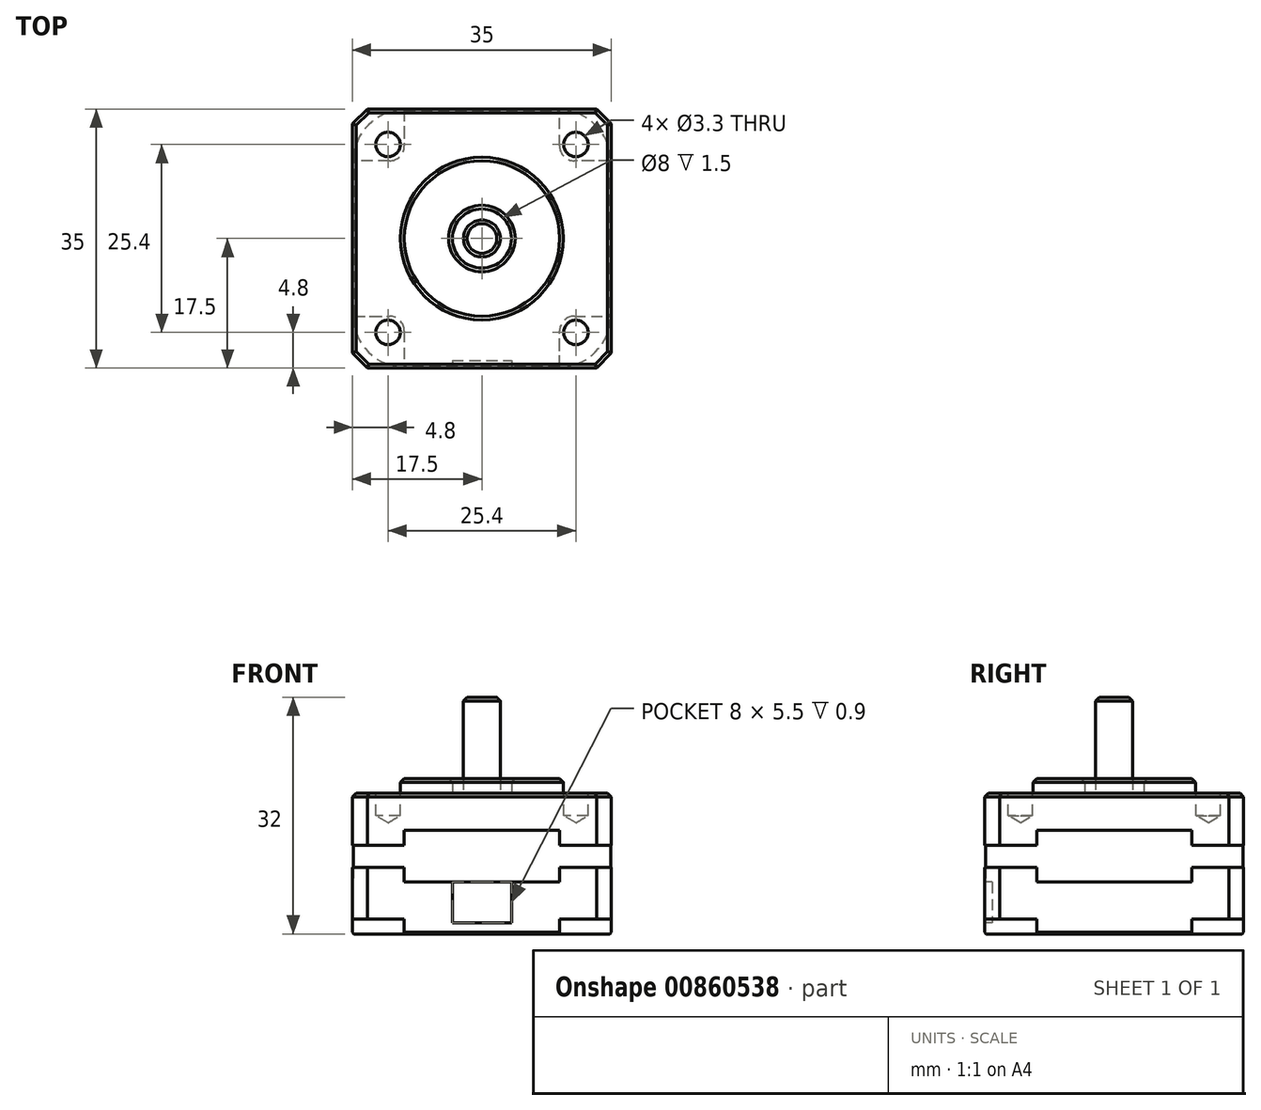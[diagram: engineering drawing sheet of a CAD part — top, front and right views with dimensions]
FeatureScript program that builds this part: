
annotation { "Feature Type Name" : "Feature", "Feature Type Description" : "" }
export const myFeature = defineFeature(function(context is Context, id is Id, definition is map)
    precondition{}
    {
        {
            var Q0;
            Q0=qCreatedBy(makeId("Top.planeOp"),FACE);
            var sketch = newSketch(context, id + "F0", { "sketchPlane" : qUnion([Q0])});
            skLineSegment(sketch, "E0.bottom", {"start": v(-17.5, 17.5) * mm, "end": v(17.5, 17.5) * mm});
            skLineSegment(sketch, "E0.top", {"start": v(-17.5, -17.5) * mm, "end": v(17.5, -17.5) * mm});
            skLineSegment(sketch, "E0.left", {"start": v(-17.5, 17.5) * mm, "end": v(-17.5, -17.5) * mm});
            skLineSegment(sketch, "E0.right", {"start": v(17.5, 17.5) * mm, "end": v(17.5, -17.5) * mm});
            skSolve(sketch);
        }
        {
            var Q0;
            Q0=makeQuery(id+"F0.imprint","IMPRINT",FACE,{"disambiguationData":[TD([[makeQuery(id+"F0.imprint","IMPRINT",EDGE,{"derivedFrom":sQuery(id+"F0.wireOp",EDGE,"E0.bottom")}),-1.0]])]});
            extrude(context, id + "F1", {"entities" : qUnion([Q0]), "depth" : 5 * mm, "offsetDistance" : 25 * mm});
        }
        {
            var Q0;
            Q0=makeQuery(id+"F1.opExtrude","CAP_FACE",FACE,{"disambiguationData":[OSD([sQuery(id+"F0.wireOp",EDGE,"E0.bottom"),sQuery(id+"F0.wireOp",EDGE,"E0.top"),sQuery(id+"F0.wireOp",EDGE,"E0.left"),sQuery(id+"F0.wireOp",EDGE,"E0.right")])],"isStart":false});
            var sketch = newSketch(context, id + "F2", { "sketchPlane" : qUnion([Q0])});
            skCircle(sketch, "E1", {"center": v(0, 0) * mm, "radius": 11 * mm});
            skCircle(sketch, "E2", {"center": v(0, 0) * mm, "radius": 4 * mm});
            skSolve(sketch);
        }
        {
            var Q0;
            Q0=makeQuery(id+"F2.imprint","IMPRINT",FACE,{"disambiguationData":[TD([[makeQuery(id+"F2.imprint","IMPRINT",EDGE,{"derivedFrom":sQuery(id+"F2.wireOp",EDGE,"E1")}),1.0]])]});
            extrude(context, id + "F3", {"entities" : qUnion([Q0]), "operationType" : NewBodyOperationType.ADD, "depth" : 2 * mm, "offsetDistance" : 25 * mm});
        }
        {
            var Q0;
            Q0=makeQuery(id+"F1.opExtrude","SWEPT_EDGE",EDGE,{"disambiguationData":[OSD([sQuery(id+"F0.wireOp",EDGE,"E0.bottom"),sQuery(id+"F0.wireOp",EDGE,"E0.left")])]});
            var Q1;
            Q1=makeQuery(id+"F1.opExtrude","SWEPT_EDGE",EDGE,{"disambiguationData":[OSD([sQuery(id+"F0.wireOp",EDGE,"E0.top"),sQuery(id+"F0.wireOp",EDGE,"E0.left")])]});
            var Q2;
            Q2=makeQuery(id+"F1.opExtrude","SWEPT_EDGE",EDGE,{"disambiguationData":[OSD([sQuery(id+"F0.wireOp",EDGE,"E0.top"),sQuery(id+"F0.wireOp",EDGE,"E0.right")])]});
            var Q3;
            Q3=makeQuery(id+"F1.opExtrude","SWEPT_EDGE",EDGE,{"disambiguationData":[OSD([sQuery(id+"F0.wireOp",EDGE,"E0.bottom"),sQuery(id+"F0.wireOp",EDGE,"E0.right")])]});
            chamfer(context, id + "F4", {"entities" : qUnion([Q0, Q1, Q2, Q3]), "width" : 2 * mm, "tangentPropagation" : true});
        }
        {
            var Q0;
            Q0=makeQuery(id+"F3.boolean.opBoolean","SPLIT",FACE,{"disambiguationData":[TD([makeQuery(id+"F3.opExtrude","SWEPT_FACE",FACE,{"disambiguationData":[OSD([sQuery(id+"F2.wireOp",EDGE,"E2")])]})])],"derivedFrom":makeQuery(id+"F1.opExtrude","CAP_FACE",FACE,{"disambiguationData":[OSD([sQuery(id+"F0.wireOp",EDGE,"E0.bottom"),sQuery(id+"F0.wireOp",EDGE,"E0.top"),sQuery(id+"F0.wireOp",EDGE,"E0.left"),sQuery(id+"F0.wireOp",EDGE,"E0.right")])],"isStart":false})});
            var sketch = newSketch(context, id + "F5", { "sketchPlane" : qUnion([Q0])});
            skCircle(sketch, "E3", {"center": v(0, 0) * mm, "radius": 2.5 * mm});
            skSolve(sketch);
        }
        {
            var Q0;
            Q0=makeQuery(id+"F5.imprint","IMPRINT",FACE,{"disambiguationData":[TD([[makeQuery(id+"F5.imprint","IMPRINT",EDGE,{"derivedFrom":sQuery(id+"F5.wireOp",EDGE,"E3")}),1.0]])]});
            extrude(context, id + "F6", {"entities" : qUnion([Q0]), "operationType" : NewBodyOperationType.ADD, "depth" : 13 * mm, "offsetDistance" : 25 * mm});
        }
        {
            var Q0;
            {var subQ0=sQuery(id+"F0.wireOp",EDGE,"E0.left");var subQ1=sQuery(id+"F0.wireOp",EDGE,"E0.top");var subQ2=sQuery(id+"F0.wireOp",EDGE,"E0.right");var subQ3=sQuery(id+"F0.wireOp",EDGE,"E0.bottom");Q0=makeQuery(id+"F3.boolean.opBoolean","SPLIT",FACE,{"disambiguationData":[TD([makeQuery(id+"F1.opExtrude","SWEPT_FACE",FACE,{"disambiguationData":[OSD([subQ3])]})])],"derivedFrom":makeQuery(id+"F1.opExtrude","CAP_FACE",FACE,{"disambiguationData":[OSD([subQ3,subQ1,subQ0,subQ2])],"isStart":false})});}
            var sketch = newSketch(context, id + "F7", { "sketchPlane" : qUnion([Q0])});
            skPoint(sketch, "E4", {"position": v(-12.7, -12.7) * mm});
            skPoint(sketch, "E5", {"position": v(-12.7, 12.7) * mm});
            skPoint(sketch, "E6", {"position": v(12.7, 12.7) * mm});
            skPoint(sketch, "E7", {"position": v(12.7, -12.7) * mm});
            skSolve(sketch);
        }
        {
            var Q0;
            Q0=sQuery(id+"F7.wireOp",VERTEX,"E4");
            var Q1;
            Q1=sQuery(id+"F7.wireOp",VERTEX,"E5");
            var Q2;
            Q2=sQuery(id+"F7.wireOp",VERTEX,"E6");
            var Q3;
            Q3=sQuery(id+"F7.wireOp",VERTEX,"E7");
            var Q4;
            Q4=makeQuery(id+"F1.opExtrude","SWEPT_BODY",BODY,{"disambiguationData":[OSD([sQuery(id+"F0.wireOp",EDGE,"E0.bottom"),sQuery(id+"F0.wireOp",EDGE,"E0.top"),sQuery(id+"F0.wireOp",EDGE,"E0.left"),sQuery(id+"F0.wireOp",EDGE,"E0.right")])]});
            hole(context, id + "F8", {"style" : HoleStyle.SIMPLE, "endStyle" : HoleEndStyle.BLIND, "standardTappedOrClearance" : lookupTablePath({ "standard" : "ISO", "engagement" : "75%", "pitch" : "0.7 mm", "size" : "M4", "type" : "Tapped" }), "standardBlindInLast" : lookupTablePath({ "standard" : "ISO", "engagement" : "75%", "pitch" : "0.7 mm", "size" : "M4", "type" : "Tapped" }), "holeDiameter" : 3.3 * mm, "majorDiameter" : 4 * mm, "showTappedDepth" : true, "holeDepth" : 3 * mm, "isTappedThrough" : true, "tappedDepth" : 0.9 * mm, "tapClearance" : 3, "locations" : qUnion([Q0, Q1, Q2, Q3]), "scope" : qUnion([Q4])});
        }
        {
            var Q0;
            Q0=makeQuery(id+"F1.opExtrude","CAP_EDGE",EDGE,{"disambiguationData":[OSD([sQuery(id+"F0.wireOp",EDGE,"E0.top")])],"isStart":false});
            var Q1;
            Q1=makeQuery(id+"F1.opExtrude","CAP_EDGE",EDGE,{"disambiguationData":[OSD([sQuery(id+"F0.wireOp",EDGE,"E0.left")])],"isStart":false});
            var Q2;
            Q2=makeQuery(id+"F1.opExtrude","CAP_EDGE",EDGE,{"disambiguationData":[OSD([sQuery(id+"F0.wireOp",EDGE,"E0.bottom")])],"isStart":false});
            var Q3;
            Q3=makeQuery(id+"F1.opExtrude","CAP_EDGE",EDGE,{"disambiguationData":[OSD([sQuery(id+"F0.wireOp",EDGE,"E0.right")])],"isStart":false});
            var Q4;
            {var subQ0=sQuery(id+"F0.wireOp",EDGE,"E0.left");var subQ1=sQuery(id+"F0.wireOp",EDGE,"E0.top");var subQ2=sQuery(id+"F0.wireOp",EDGE,"E0.right");var subQ3=sQuery(id+"F0.wireOp",EDGE,"E0.bottom");Q4=makeQuery(id+"F4.opChamfer","BLEND_EDGE",EDGE,{"blendedFrom":[makeQuery(id+"F1.opExtrude","SWEPT_EDGE",EDGE,{"disambiguationData":[OSD([subQ1,subQ2])]}),makeQuery(id+"F3.boolean.opBoolean","SPLIT",FACE,{"disambiguationData":[TD([makeQuery(id+"F1.opExtrude","SWEPT_FACE",FACE,{"disambiguationData":[OSD([subQ3])]})])],"derivedFrom":makeQuery(id+"F1.opExtrude","CAP_FACE",FACE,{"disambiguationData":[OSD([subQ3,subQ1,subQ0,subQ2])],"isStart":false})})],"blendedInto":[makeQuery(id+"F3.boolean.opBoolean","SPLIT",FACE,{"disambiguationData":[TD([makeQuery(id+"F1.opExtrude","SWEPT_FACE",FACE,{"disambiguationData":[OSD([subQ3])]})])],"derivedFrom":makeQuery(id+"F1.opExtrude","CAP_FACE",FACE,{"disambiguationData":[OSD([subQ3,subQ1,subQ0,subQ2])],"isStart":false})})]});}
            var Q5;
            {var subQ0=sQuery(id+"F0.wireOp",EDGE,"E0.left");var subQ1=sQuery(id+"F0.wireOp",EDGE,"E0.top");var subQ2=sQuery(id+"F0.wireOp",EDGE,"E0.right");var subQ3=sQuery(id+"F0.wireOp",EDGE,"E0.bottom");Q5=makeQuery(id+"F4.opChamfer","BLEND_EDGE",EDGE,{"blendedFrom":[makeQuery(id+"F1.opExtrude","SWEPT_EDGE",EDGE,{"disambiguationData":[OSD([subQ3,subQ2])]}),makeQuery(id+"F3.boolean.opBoolean","SPLIT",FACE,{"disambiguationData":[TD([makeQuery(id+"F1.opExtrude","SWEPT_FACE",FACE,{"disambiguationData":[OSD([subQ3])]})])],"derivedFrom":makeQuery(id+"F1.opExtrude","CAP_FACE",FACE,{"disambiguationData":[OSD([subQ3,subQ1,subQ0,subQ2])],"isStart":false})})],"blendedInto":[makeQuery(id+"F3.boolean.opBoolean","SPLIT",FACE,{"disambiguationData":[TD([makeQuery(id+"F1.opExtrude","SWEPT_FACE",FACE,{"disambiguationData":[OSD([subQ3])]})])],"derivedFrom":makeQuery(id+"F1.opExtrude","CAP_FACE",FACE,{"disambiguationData":[OSD([subQ3,subQ1,subQ0,subQ2])],"isStart":false})})]});}
            var Q6;
            {var subQ0=sQuery(id+"F0.wireOp",EDGE,"E0.left");var subQ1=sQuery(id+"F0.wireOp",EDGE,"E0.top");var subQ2=sQuery(id+"F0.wireOp",EDGE,"E0.right");var subQ3=sQuery(id+"F0.wireOp",EDGE,"E0.bottom");Q6=makeQuery(id+"F4.opChamfer","BLEND_EDGE",EDGE,{"blendedFrom":[makeQuery(id+"F1.opExtrude","SWEPT_EDGE",EDGE,{"disambiguationData":[OSD([subQ3,subQ0])]}),makeQuery(id+"F3.boolean.opBoolean","SPLIT",FACE,{"disambiguationData":[TD([makeQuery(id+"F1.opExtrude","SWEPT_FACE",FACE,{"disambiguationData":[OSD([subQ3])]})])],"derivedFrom":makeQuery(id+"F1.opExtrude","CAP_FACE",FACE,{"disambiguationData":[OSD([subQ3,subQ1,subQ0,subQ2])],"isStart":false})})],"blendedInto":[makeQuery(id+"F3.boolean.opBoolean","SPLIT",FACE,{"disambiguationData":[TD([makeQuery(id+"F1.opExtrude","SWEPT_FACE",FACE,{"disambiguationData":[OSD([subQ3])]})])],"derivedFrom":makeQuery(id+"F1.opExtrude","CAP_FACE",FACE,{"disambiguationData":[OSD([subQ3,subQ1,subQ0,subQ2])],"isStart":false})})]});}
            var Q7;
            {var subQ0=sQuery(id+"F0.wireOp",EDGE,"E0.left");var subQ1=sQuery(id+"F0.wireOp",EDGE,"E0.top");var subQ2=sQuery(id+"F0.wireOp",EDGE,"E0.right");var subQ3=sQuery(id+"F0.wireOp",EDGE,"E0.bottom");Q7=makeQuery(id+"F4.opChamfer","BLEND_EDGE",EDGE,{"blendedFrom":[makeQuery(id+"F1.opExtrude","SWEPT_EDGE",EDGE,{"disambiguationData":[OSD([subQ1,subQ0])]}),makeQuery(id+"F3.boolean.opBoolean","SPLIT",FACE,{"disambiguationData":[TD([makeQuery(id+"F1.opExtrude","SWEPT_FACE",FACE,{"disambiguationData":[OSD([subQ3])]})])],"derivedFrom":makeQuery(id+"F1.opExtrude","CAP_FACE",FACE,{"disambiguationData":[OSD([subQ3,subQ1,subQ0,subQ2])],"isStart":false})})],"blendedInto":[makeQuery(id+"F3.boolean.opBoolean","SPLIT",FACE,{"disambiguationData":[TD([makeQuery(id+"F1.opExtrude","SWEPT_FACE",FACE,{"disambiguationData":[OSD([subQ3])]})])],"derivedFrom":makeQuery(id+"F1.opExtrude","CAP_FACE",FACE,{"disambiguationData":[OSD([subQ3,subQ1,subQ0,subQ2])],"isStart":false})})]});}
            var Q8;
            Q8=makeQuery(id+"F3.opExtrude","CAP_EDGE",EDGE,{"disambiguationData":[OSD([sQuery(id+"F2.wireOp",EDGE,"E1")])],"isStart":false});
            var Q9;
            Q9=makeQuery(id+"F3.opExtrude","CAP_EDGE",EDGE,{"disambiguationData":[OSD([sQuery(id+"F2.wireOp",EDGE,"E2")])],"isStart":false});
            var Q10;
            Q10=makeQuery(id+"F6.opExtrude","CAP_EDGE",EDGE,{"disambiguationData":[OSD([sQuery(id+"F5.wireOp",EDGE,"E3")])],"isStart":false});
            chamfer(context, id + "F9", {"entities" : qUnion([Q0, Q1, Q2, Q3, Q4, Q5, Q6, Q7, Q8, Q9, Q10]), "width" : 0.5 * mm, "tangentPropagation" : true});
        }
        {
            var Q0;
            Q0=makeQuery(id+"F1.opExtrude","CAP_FACE",FACE,{"disambiguationData":[OSD([sQuery(id+"F0.wireOp",EDGE,"E0.bottom"),sQuery(id+"F0.wireOp",EDGE,"E0.top"),sQuery(id+"F0.wireOp",EDGE,"E0.left"),sQuery(id+"F0.wireOp",EDGE,"E0.right")])],"isStart":true});
            var sketch = newSketch(context, id + "F10", { "sketchPlane" : qUnion([Q0])});
            skLineSegment(sketch, "E8.bottom", {"start": v(-10.4, 17.4) * mm, "end": v(10.4, 17.4) * mm});
            skLineSegment(sketch, "E8.top", {"start": v(-10.4, -17.4) * mm, "end": v(10.4, -17.4) * mm});
            skLineSegment(sketch, "E8.left", {"start": v(-17.4, 10.4) * mm, "end": v(-17.4, -10.4) * mm});
            skLineSegment(sketch, "E8.right", {"start": v(17.4, 10.4) * mm, "end": v(17.4, -10.4) * mm});
            skPoint(sketch, "E9.visualSharp", {"position": v(-17.4, 17.4) * mm});
            skArc(sketch, "E9.filletArc", {"start": v(-10.4, 17.4) * mm, "mid": v(-15.35, 15.35) * mm, "end": v(-17.4, 10.4) * mm});
            skPoint(sketch, "E10.visualSharp", {"position": v(17.4, 17.4) * mm});
            skArc(sketch, "E10.filletArc", {"start": v(17.4, 10.4) * mm, "mid": v(15.35, 15.35) * mm, "end": v(10.4, 17.4) * mm});
            skPoint(sketch, "E11.visualSharp", {"position": v(17.4, -17.4) * mm});
            skArc(sketch, "E11.filletArc", {"start": v(10.4, -17.4) * mm, "mid": v(15.35, -15.35) * mm, "end": v(17.4, -10.4) * mm});
            skPoint(sketch, "E12.visualSharp", {"position": v(-17.4, -17.4) * mm});
            skArc(sketch, "E12.filletArc", {"start": v(-17.4, -10.4) * mm, "mid": v(-15.35, -15.35) * mm, "end": v(-10.4, -17.4) * mm});
            skSolve(sketch);
        }
        {
            var Q0;
            Q0=makeQuery(id+"F10.imprint","IMPRINT",FACE,{"disambiguationData":[TD([[makeQuery(id+"F10.imprint","IMPRINT",EDGE,{"derivedFrom":sQuery(id+"F10.wireOp",EDGE,"E8.bottom")}),-1.0]])]});
            extrude(context, id + "F11", {"entities" : qUnion([Q0]), "operationType" : NewBodyOperationType.ADD, "depth" : 7 * mm, "offsetDistance" : 25 * mm});
        }
        {
            var Q0;
            Q0=makeQuery(id+"F1.opExtrude","CAP_FACE",FACE,{"disambiguationData":[OSD([sQuery(id+"F0.wireOp",EDGE,"E0.bottom"),sQuery(id+"F0.wireOp",EDGE,"E0.top"),sQuery(id+"F0.wireOp",EDGE,"E0.left"),sQuery(id+"F0.wireOp",EDGE,"E0.right")])],"isStart":true});
            var sketch = newSketch(context, id + "F12", { "sketchPlane" : qUnion([Q0])});
            skLineSegment(sketch, "E13.bottom", {"start": v(-17.5, 17.5) * mm, "end": v(-10.5, 17.5) * mm});
            skLineSegment(sketch, "E13.top", {"start": v(-17.5, 10.5) * mm, "end": v(-10.5, 10.5) * mm});
            skLineSegment(sketch, "E13.left", {"start": v(-17.5, 17.5) * mm, "end": v(-17.5, 10.5) * mm});
            skLineSegment(sketch, "E13.right", {"start": v(-10.5, 17.5) * mm, "end": v(-10.5, 10.5) * mm});
            skLineSegment(sketch, "E14", {"start": v(-17.5, 15.5) * mm, "end": v(-15.5, 17.5) * mm});
            skLineSegment(sketch, "E15.1.0", {"start": v(-15.5, -17.5) * mm, "end": v(-17.5, -15.5) * mm});
            skLineSegment(sketch, "E15.1.1", {"start": v(-17.5, -10.5) * mm, "end": v(-10.5, -10.5) * mm});
            skLineSegment(sketch, "E15.1.2", {"start": v(-17.5, -17.5) * mm, "end": v(-17.5, -10.5) * mm});
            skLineSegment(sketch, "E15.1.3", {"start": v(-17.5, -17.5) * mm, "end": v(-10.5, -17.5) * mm});
            skLineSegment(sketch, "E15.1.4", {"start": v(-10.5, -17.5) * mm, "end": v(-10.5, -10.5) * mm});
            skLineSegment(sketch, "E15.2.0", {"start": v(17.5, -15.5) * mm, "end": v(15.5, -17.5) * mm});
            skLineSegment(sketch, "E15.2.1", {"start": v(10.5, -17.5) * mm, "end": v(10.5, -10.5) * mm});
            skLineSegment(sketch, "E15.2.2", {"start": v(17.5, -17.5) * mm, "end": v(10.5, -17.5) * mm});
            skLineSegment(sketch, "E15.2.3", {"start": v(17.5, -17.5) * mm, "end": v(17.5, -10.5) * mm});
            skLineSegment(sketch, "E15.2.4", {"start": v(17.5, -10.5) * mm, "end": v(10.5, -10.5) * mm});
            skLineSegment(sketch, "E15.3.0", {"start": v(15.5, 17.5) * mm, "end": v(17.5, 15.5) * mm});
            skLineSegment(sketch, "E15.3.1", {"start": v(17.5, 10.5) * mm, "end": v(10.5, 10.5) * mm});
            skLineSegment(sketch, "E15.3.2", {"start": v(17.5, 17.5) * mm, "end": v(17.5, 10.5) * mm});
            skLineSegment(sketch, "E15.3.3", {"start": v(17.5, 17.5) * mm, "end": v(10.5, 17.5) * mm});
            skLineSegment(sketch, "E15.3.4", {"start": v(10.5, 17.5) * mm, "end": v(10.5, 10.5) * mm});
            skPoint(sketch, "E15.center", {"position": v(0, 0) * mm});
            skSolve(sketch);
        }
        {
            var Q0;
            {var subQ9=sQuery(id+"F12.wireOp",EDGE,"E14");Q0=makeQuery(id+"F12.imprint","IMPRINT",FACE,{"disambiguationData":[TD([[makeQuery(id+"F12.imprint","IMPRINT",EDGE,{"derivedFrom":subQ9}),1.0]])]});}
            var Q1;
            {var subQ1=sQuery(id+"F12.wireOp",EDGE,"E15.3.0");Q1=makeQuery(id+"F12.imprint","IMPRINT",FACE,{"disambiguationData":[TD([[makeQuery(id+"F12.imprint","IMPRINT",EDGE,{"derivedFrom":subQ1}),1.0]])]});}
            var Q2;
            {var subQ1=sQuery(id+"F12.wireOp",EDGE,"E15.2.0");Q2=makeQuery(id+"F12.imprint","IMPRINT",FACE,{"disambiguationData":[TD([[makeQuery(id+"F12.imprint","IMPRINT",EDGE,{"derivedFrom":subQ1}),1.0]])]});}
            var Q3;
            {var subQ1=sQuery(id+"F12.wireOp",EDGE,"E15.1.0");Q3=makeQuery(id+"F12.imprint","IMPRINT",FACE,{"disambiguationData":[TD([[makeQuery(id+"F12.imprint","IMPRINT",EDGE,{"derivedFrom":subQ1}),1.0]])]});}
            extrude(context, id + "F13", {"entities" : qUnion([Q0, Q1, Q2, Q3]), "operationType" : NewBodyOperationType.ADD, "depth" : 2 * mm, "offsetDistance" : 25 * mm});
        }
        {
            var Q0;
            Q0=makeQuery(id+"F11.opExtrude","CAP_FACE",FACE,{"disambiguationData":[OSD([sQuery(id+"F10.wireOp",EDGE,"E8.bottom"),sQuery(id+"F10.wireOp",EDGE,"E8.top"),sQuery(id+"F10.wireOp",EDGE,"E8.left"),sQuery(id+"F10.wireOp",EDGE,"E8.right"),sQuery(id+"F10.wireOp",EDGE,"E9.filletArc"),sQuery(id+"F10.wireOp",EDGE,"E10.filletArc"),sQuery(id+"F10.wireOp",EDGE,"E11.filletArc"),sQuery(id+"F10.wireOp",EDGE,"E12.filletArc")])],"isStart":false});
            var sketch = newSketch(context, id + "F14", { "sketchPlane" : qUnion([Q0])});
            skLineSegment(sketch, "E16.bottom", {"start": v(-17.5, 17.5) * mm, "end": v(17.5, 17.5) * mm});
            skLineSegment(sketch, "E16.top", {"start": v(-17.5, -17.5) * mm, "end": v(17.5, -17.5) * mm});
            skLineSegment(sketch, "E16.left", {"start": v(-17.5, 17.5) * mm, "end": v(-17.5, -17.5) * mm});
            skLineSegment(sketch, "E16.right", {"start": v(17.5, 17.5) * mm, "end": v(17.5, -17.5) * mm});
            skSolve(sketch);
        }
        {
            var Q0;
            Q0=makeQuery(id+"F14.imprint","IMPRINT",FACE,{"disambiguationData":[TD([[makeQuery(id+"F14.imprint","IMPRINT",EDGE,{"derivedFrom":sQuery(id+"F14.wireOp",EDGE,"E16.bottom")}),-1.0]])]});
            var Q1;
            Q1=makeQuery(id+"F14.imprint","IMPRINT",FACE,{"disambiguationData":[TD([[makeQuery(id+"F14.imprint","IMPRINT",EDGE,{"derivedFrom":makeQuery(id+"F11.opExtrude","CAP_EDGE",EDGE,{"disambiguationData":[OSD([sQuery(id+"F10.wireOp",EDGE,"E8.bottom")])],"isStart":false})}),-1.0]])]});
            extrude(context, id + "F15", {"entities" : qUnion([Q0, Q1]), "operationType" : NewBodyOperationType.ADD, "depth" : 7 * mm, "offsetDistance" : 25 * mm});
        }
        {
            var Q0;
            Q0=makeQuery(id+"F15.opExtrude","SWEPT_EDGE",EDGE,{"disambiguationData":[OSD([sQuery(id+"F14.wireOp",EDGE,"E16.bottom"),sQuery(id+"F14.wireOp",EDGE,"E16.left")])]});
            var Q1;
            Q1=makeQuery(id+"F15.opExtrude","SWEPT_EDGE",EDGE,{"disambiguationData":[OSD([sQuery(id+"F14.wireOp",EDGE,"E16.bottom"),sQuery(id+"F14.wireOp",EDGE,"E16.right")])]});
            var Q2;
            Q2=makeQuery(id+"F15.opExtrude","SWEPT_EDGE",EDGE,{"disambiguationData":[OSD([sQuery(id+"F14.wireOp",EDGE,"E16.top"),sQuery(id+"F14.wireOp",EDGE,"E16.right")])]});
            var Q3;
            Q3=makeQuery(id+"F15.opExtrude","SWEPT_EDGE",EDGE,{"disambiguationData":[OSD([sQuery(id+"F14.wireOp",EDGE,"E16.top"),sQuery(id+"F14.wireOp",EDGE,"E16.left")])]});
            chamfer(context, id + "F16", {"entities" : qUnion([Q0, Q1, Q2, Q3]), "width" : 2 * mm, "tangentPropagation" : true});
        }
        {
            var Q0;
            Q0=makeQuery(id+"F15.opExtrude","CAP_FACE",FACE,{"disambiguationData":[OSD([sQuery(id+"F14.wireOp",EDGE,"E16.bottom"),sQuery(id+"F14.wireOp",EDGE,"E16.top"),sQuery(id+"F14.wireOp",EDGE,"E16.left"),sQuery(id+"F14.wireOp",EDGE,"E16.right")])],"isStart":true});
            var sketch = newSketch(context, id + "F17", { "sketchPlane" : qUnion([Q0])});
            skLineSegment(sketch, "E17.bottom", {"start": v(-17.5, 17.5) * mm, "end": v(-10.5, 17.5) * mm});
            skLineSegment(sketch, "E17.top", {"start": v(-17.5, 10.5) * mm, "end": v(-10.5, 10.5) * mm});
            skLineSegment(sketch, "E17.left", {"start": v(-17.5, 17.5) * mm, "end": v(-17.5, 10.5) * mm});
            skLineSegment(sketch, "E17.right", {"start": v(-10.5, 17.5) * mm, "end": v(-10.5, 10.5) * mm});
            skLineSegment(sketch, "E18", {"start": v(-15.5, 17.5) * mm, "end": v(-17.5, 15.5) * mm});
            skLineSegment(sketch, "E19.1.0", {"start": v(-17.5, -17.5) * mm, "end": v(-17.5, -10.5) * mm});
            skLineSegment(sketch, "E19.1.1", {"start": v(-17.5, -17.5) * mm, "end": v(-10.5, -17.5) * mm});
            skLineSegment(sketch, "E19.1.2", {"start": v(-17.5, -15.5) * mm, "end": v(-15.5, -17.5) * mm});
            skLineSegment(sketch, "E19.1.3", {"start": v(-17.5, -10.5) * mm, "end": v(-10.5, -10.5) * mm});
            skLineSegment(sketch, "E19.1.4", {"start": v(-10.5, -17.5) * mm, "end": v(-10.5, -10.5) * mm});
            skLineSegment(sketch, "E19.2.0", {"start": v(17.5, -17.5) * mm, "end": v(10.5, -17.5) * mm});
            skLineSegment(sketch, "E19.2.1", {"start": v(17.5, -17.5) * mm, "end": v(17.5, -10.5) * mm});
            skLineSegment(sketch, "E19.2.2", {"start": v(15.5, -17.5) * mm, "end": v(17.5, -15.5) * mm});
            skLineSegment(sketch, "E19.2.3", {"start": v(10.5, -17.5) * mm, "end": v(10.5, -10.5) * mm});
            skLineSegment(sketch, "E19.2.4", {"start": v(17.5, -10.5) * mm, "end": v(10.5, -10.5) * mm});
            skLineSegment(sketch, "E19.3.0", {"start": v(17.5, 17.5) * mm, "end": v(17.5, 10.5) * mm});
            skLineSegment(sketch, "E19.3.1", {"start": v(17.5, 17.5) * mm, "end": v(10.5, 17.5) * mm});
            skLineSegment(sketch, "E19.3.2", {"start": v(17.5, 15.5) * mm, "end": v(15.5, 17.5) * mm});
            skLineSegment(sketch, "E19.3.3", {"start": v(17.5, 10.5) * mm, "end": v(10.5, 10.5) * mm});
            skLineSegment(sketch, "E19.3.4", {"start": v(10.5, 17.5) * mm, "end": v(10.5, 10.5) * mm});
            skPoint(sketch, "E19.center", {"position": v(0, 0) * mm});
            skSolve(sketch);
        }
        {
            var Q0;
            {var subQ5=sQuery(id+"F17.wireOp",EDGE,"E19.3.2");Q0=makeQuery(id+"F17.imprint","IMPRINT",FACE,{"disambiguationData":[TD([[makeQuery(id+"F17.imprint","IMPRINT",EDGE,{"derivedFrom":subQ5}),1.0]])]});}
            var Q1;
            {var subQ9=sQuery(id+"F17.wireOp",EDGE,"E18");Q1=makeQuery(id+"F17.imprint","IMPRINT",FACE,{"disambiguationData":[TD([[makeQuery(id+"F17.imprint","IMPRINT",EDGE,{"derivedFrom":subQ9}),1.0]])]});}
            var Q2;
            {var subQ0=sQuery(id+"F17.wireOp",EDGE,"E19.1.2");Q2=makeQuery(id+"F17.imprint","IMPRINT",FACE,{"disambiguationData":[TD([[makeQuery(id+"F17.imprint","IMPRINT",EDGE,{"derivedFrom":subQ0}),1.0]])]});}
            var Q3;
            {var subQ5=sQuery(id+"F17.wireOp",EDGE,"E19.2.2");Q3=makeQuery(id+"F17.imprint","IMPRINT",FACE,{"disambiguationData":[TD([[makeQuery(id+"F17.imprint","IMPRINT",EDGE,{"derivedFrom":subQ5}),1.0]])]});}
            extrude(context, id + "F18", {"entities" : qUnion([Q0, Q1, Q2, Q3]), "operationType" : NewBodyOperationType.ADD, "depth" : 2 * mm, "offsetDistance" : 25 * mm});
        }
        {
            var Q0;
            Q0=makeQuery(id+"F18.boolean.opBoolean","MERGE",FACE,{"derivedFrom":[makeQuery(id+"F15.opExtrude","SWEPT_FACE",FACE,{"disambiguationData":[OSD([sQuery(id+"F14.wireOp",EDGE,"E16.bottom")])]}),makeQuery(id+"F18.opExtrude","SWEPT_FACE",FACE,{"disambiguationData":[OSD([sQuery(id+"F17.wireOp",EDGE,"E19.1.1")])]}),makeQuery(id+"F18.opExtrude","SWEPT_FACE",FACE,{"disambiguationData":[OSD([sQuery(id+"F17.wireOp",EDGE,"E19.2.0")])]})]});
            var sketch = newSketch(context, id + "F19", { "sketchPlane" : qUnion([Q0])});
            skLineSegment(sketch, "E20.bottom", {"start": v(-4, -7) * mm, "end": v(4, -7) * mm});
            skLineSegment(sketch, "E20.top", {"start": v(-4, -12.5) * mm, "end": v(4, -12.5) * mm});
            skLineSegment(sketch, "E20.left", {"start": v(-4, -7) * mm, "end": v(-4, -12.5) * mm});
            skLineSegment(sketch, "E20.right", {"start": v(4, -7) * mm, "end": v(4, -12.5) * mm});
            skSolve(sketch);
        }
        {
            var Q0;
            Q0=makeQuery(id+"F19.imprint","IMPRINT",FACE,{"disambiguationData":[TD([[makeQuery(id+"F19.imprint","IMPRINT",EDGE,{"derivedFrom":sQuery(id+"F19.wireOp",EDGE,"E20.bottom")}),-1.0]])]});
            extrude(context, id + "F20", {"entities" : qUnion([Q0]), "operationType" : NewBodyOperationType.REMOVE, "oppositeDirection" : true, "depth" : 1 * mm, "offsetDistance" : 25 * mm});
        }
        {
            var Q0;
            Q0=makeQuery(id+"F15.opExtrude","CAP_FACE",FACE,{"disambiguationData":[OSD([sQuery(id+"F14.wireOp",EDGE,"E16.bottom"),sQuery(id+"F14.wireOp",EDGE,"E16.top"),sQuery(id+"F14.wireOp",EDGE,"E16.left"),sQuery(id+"F14.wireOp",EDGE,"E16.right")])],"isStart":false});
            var sketch = newSketch(context, id + "F21", { "sketchPlane" : qUnion([Q0])});
            skLineSegment(sketch, "E21.bottom", {"start": v(-17.5, 10.5) * mm, "end": v(-12.5, 10.5) * mm});
            skLineSegment(sketch, "E21.top", {"start": v(-17.5, 17.5) * mm, "end": v(-10.5, 17.5) * mm});
            skLineSegment(sketch, "E21.left", {"start": v(-17.5, 10.5) * mm, "end": v(-17.5, 17.5) * mm});
            skLineSegment(sketch, "E21.right", {"start": v(-10.5, 12.5) * mm, "end": v(-10.5, 17.5) * mm});
            skPoint(sketch, "E22.visualSharp", {"position": v(-10.5, 10.5) * mm});
            skArc(sketch, "E22.filletArc", {"start": v(-12.5, 10.5) * mm, "mid": v(-11.09, 11.09) * mm, "end": v(-10.5, 12.5) * mm});
            skLineSegment(sketch, "E23.1.0", {"start": v(-10.5, -17.5) * mm, "end": v(-10.5, -12.5) * mm});
            skArc(sketch, "E23.1.1", {"start": v(-10.5, -12.5) * mm, "mid": v(-11.09, -11.09) * mm, "end": v(-12.5, -10.5) * mm});
            skLineSegment(sketch, "E23.1.2", {"start": v(-12.5, -10.5) * mm, "end": v(-17.5, -10.5) * mm});
            skLineSegment(sketch, "E23.1.3", {"start": v(-17.5, -17.5) * mm, "end": v(-17.5, -10.5) * mm});
            skLineSegment(sketch, "E23.1.4", {"start": v(-10.5, -17.5) * mm, "end": v(-17.5, -17.5) * mm});
            skLineSegment(sketch, "E23.2.0", {"start": v(17.5, -10.5) * mm, "end": v(12.5, -10.5) * mm});
            skArc(sketch, "E23.2.1", {"start": v(12.5, -10.5) * mm, "mid": v(11.09, -11.09) * mm, "end": v(10.5, -12.5) * mm});
            skLineSegment(sketch, "E23.2.2", {"start": v(10.5, -12.5) * mm, "end": v(10.5, -17.5) * mm});
            skLineSegment(sketch, "E23.2.3", {"start": v(17.5, -17.5) * mm, "end": v(10.5, -17.5) * mm});
            skLineSegment(sketch, "E23.2.4", {"start": v(17.5, -10.5) * mm, "end": v(17.5, -17.5) * mm});
            skLineSegment(sketch, "E23.3.0", {"start": v(10.5, 17.5) * mm, "end": v(10.5, 12.5) * mm});
            skArc(sketch, "E23.3.1", {"start": v(10.5, 12.5) * mm, "mid": v(11.09, 11.09) * mm, "end": v(12.5, 10.5) * mm});
            skLineSegment(sketch, "E23.3.2", {"start": v(12.5, 10.5) * mm, "end": v(17.5, 10.5) * mm});
            skLineSegment(sketch, "E23.3.3", {"start": v(17.5, 17.5) * mm, "end": v(17.5, 10.5) * mm});
            skLineSegment(sketch, "E23.3.4", {"start": v(10.5, 17.5) * mm, "end": v(17.5, 17.5) * mm});
            skPoint(sketch, "E23.center", {"position": v(0, 0) * mm});
            skSolve(sketch);
        }
        {
            var Q0;
            {var subQ4=sQuery(id+"F21.wireOp",EDGE,"E21.bottom");Q0=makeQuery(id+"F21.imprint","IMPRINT",FACE,{"disambiguationData":[TD([[makeQuery(id+"F21.imprint","IMPRINT",EDGE,{"derivedFrom":subQ4}),1.0]])]});}
            var Q1;
            {var subQ5=sQuery(id+"F21.wireOp",EDGE,"E23.3.0");Q1=makeQuery(id+"F21.imprint","IMPRINT",FACE,{"disambiguationData":[TD([[makeQuery(id+"F21.imprint","IMPRINT",EDGE,{"derivedFrom":subQ5}),1.0]])]});}
            var Q2;
            {var subQ5=sQuery(id+"F21.wireOp",EDGE,"E23.2.0");Q2=makeQuery(id+"F21.imprint","IMPRINT",FACE,{"disambiguationData":[TD([[makeQuery(id+"F21.imprint","IMPRINT",EDGE,{"derivedFrom":subQ5}),1.0]])]});}
            var Q3;
            {var subQ5=sQuery(id+"F21.wireOp",EDGE,"E23.1.0");Q3=makeQuery(id+"F21.imprint","IMPRINT",FACE,{"disambiguationData":[TD([[makeQuery(id+"F21.imprint","IMPRINT",EDGE,{"derivedFrom":subQ5}),1.0]])]});}
            extrude(context, id + "F22", {"entities" : qUnion([Q0, Q1, Q2, Q3]), "operationType" : NewBodyOperationType.REMOVE, "oppositeDirection" : true, "depth" : 2 * mm, "offsetDistance" : 25 * mm});
        }
        {
            var Q0;
            Q0=makeQuery(id+"F15.opExtrude","CAP_EDGE",EDGE,{"disambiguationData":[OSD([sQuery(id+"F14.wireOp",EDGE,"E16.right")])],"isStart":false});
            var Q1;
            Q1=makeQuery(id+"F15.opExtrude","CAP_EDGE",EDGE,{"disambiguationData":[OSD([sQuery(id+"F14.wireOp",EDGE,"E16.bottom")])],"isStart":false});
            var Q2;
            Q2=makeQuery(id+"F15.opExtrude","CAP_EDGE",EDGE,{"disambiguationData":[OSD([sQuery(id+"F14.wireOp",EDGE,"E16.left")])],"isStart":false});
            var Q3;
            Q3=makeQuery(id+"F15.opExtrude","CAP_EDGE",EDGE,{"disambiguationData":[OSD([sQuery(id+"F14.wireOp",EDGE,"E16.top")])],"isStart":false});
            var Q4;
            Q4=makeQuery(id+"F22.boolean.opBoolean","COPY",EDGE,{"derivedFrom":makeQuery(id+"F22.opExtrude","CAP_EDGE",EDGE,{"disambiguationData":[OSD([sQuery(id+"F21.wireOp",EDGE,"E23.2.2")])],"isStart":true})});
            var Q5;
            Q5=makeQuery(id+"F22.boolean.opBoolean","COPY",EDGE,{"derivedFrom":makeQuery(id+"F22.opExtrude","CAP_EDGE",EDGE,{"disambiguationData":[OSD([sQuery(id+"F21.wireOp",EDGE,"E23.2.1")])],"isStart":true})});
            var Q6;
            Q6=makeQuery(id+"F22.boolean.opBoolean","COPY",EDGE,{"derivedFrom":makeQuery(id+"F22.opExtrude","CAP_EDGE",EDGE,{"disambiguationData":[OSD([sQuery(id+"F21.wireOp",EDGE,"E23.2.0")])],"isStart":true})});
            var Q7;
            Q7=makeQuery(id+"F22.boolean.opBoolean","COPY",EDGE,{"derivedFrom":makeQuery(id+"F22.opExtrude","CAP_EDGE",EDGE,{"disambiguationData":[OSD([sQuery(id+"F21.wireOp",EDGE,"E23.3.2")])],"isStart":true})});
            var Q8;
            Q8=makeQuery(id+"F22.boolean.opBoolean","COPY",EDGE,{"derivedFrom":makeQuery(id+"F22.opExtrude","CAP_EDGE",EDGE,{"disambiguationData":[OSD([sQuery(id+"F21.wireOp",EDGE,"E23.3.1")])],"isStart":true})});
            var Q9;
            Q9=makeQuery(id+"F22.boolean.opBoolean","COPY",EDGE,{"derivedFrom":makeQuery(id+"F22.opExtrude","CAP_EDGE",EDGE,{"disambiguationData":[OSD([sQuery(id+"F21.wireOp",EDGE,"E23.3.0")])],"isStart":true})});
            var Q10;
            Q10=makeQuery(id+"F22.boolean.opBoolean","COPY",EDGE,{"derivedFrom":makeQuery(id+"F22.opExtrude","CAP_EDGE",EDGE,{"disambiguationData":[OSD([sQuery(id+"F21.wireOp",EDGE,"E21.right")])],"isStart":true})});
            var Q11;
            Q11=makeQuery(id+"F22.boolean.opBoolean","COPY",EDGE,{"derivedFrom":makeQuery(id+"F22.opExtrude","CAP_EDGE",EDGE,{"disambiguationData":[OSD([sQuery(id+"F21.wireOp",EDGE,"E22.filletArc")])],"isStart":true})});
            var Q12;
            Q12=makeQuery(id+"F22.boolean.opBoolean","COPY",EDGE,{"derivedFrom":makeQuery(id+"F22.opExtrude","CAP_EDGE",EDGE,{"disambiguationData":[OSD([sQuery(id+"F21.wireOp",EDGE,"E21.bottom")])],"isStart":true})});
            var Q13;
            Q13=makeQuery(id+"F22.boolean.opBoolean","COPY",EDGE,{"derivedFrom":makeQuery(id+"F22.opExtrude","CAP_EDGE",EDGE,{"disambiguationData":[OSD([sQuery(id+"F21.wireOp",EDGE,"E23.1.2")])],"isStart":true})});
            var Q14;
            Q14=makeQuery(id+"F22.boolean.opBoolean","COPY",EDGE,{"derivedFrom":makeQuery(id+"F22.opExtrude","CAP_EDGE",EDGE,{"disambiguationData":[OSD([sQuery(id+"F21.wireOp",EDGE,"E23.1.1")])],"isStart":true})});
            var Q15;
            Q15=makeQuery(id+"F22.boolean.opBoolean","COPY",EDGE,{"derivedFrom":makeQuery(id+"F22.opExtrude","CAP_EDGE",EDGE,{"disambiguationData":[OSD([sQuery(id+"F21.wireOp",EDGE,"E23.1.0")])],"isStart":true})});
            chamfer(context, id + "F23", {"entities" : qUnion([Q0, Q1, Q2, Q3, Q4, Q5, Q6, Q7, Q8, Q9, Q10, Q11, Q12, Q13, Q14, Q15]), "width" : 0.2 * mm, "tangentPropagation" : true});
        }
    });
